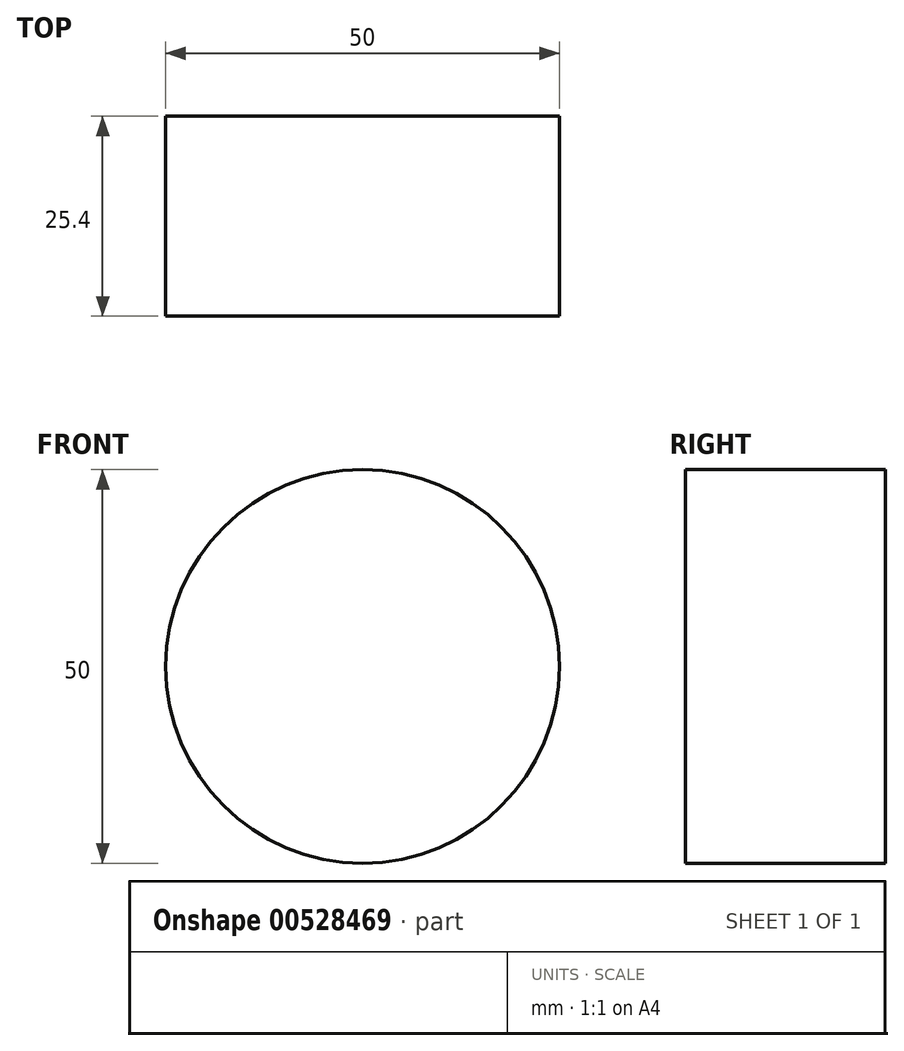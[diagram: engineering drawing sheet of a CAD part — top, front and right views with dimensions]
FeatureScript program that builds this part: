
annotation { "Feature Type Name" : "Feature", "Feature Type Description" : "" }
export const myFeature = defineFeature(function(context is Context, id is Id, definition is map)
    precondition{}
    {
        {
            var Q0;
            Q0=qCreatedBy(makeId("Front.planeOp"),FACE);
            var sketch = newSketch(context, id + "F0", { "sketchPlane" : qUnion([Q0])});
            skCircle(sketch, "E0", {"center": v(29.08, 27.37) * mm, "radius": 25 * mm});
            skSolve(sketch);
        }
        {
            var Q0;
            Q0=makeQuery(id+"F0.imprint","IMPRINT",FACE,{"disambiguationData":[TD([[makeQuery(id+"F0.imprint","IMPRINT",EDGE,{"derivedFrom":sQuery(id+"F0.wireOp",EDGE,"E0")}),1.0]])]});
            extrude(context, id + "F1", {"entities" : qUnion([Q0]), "depth" : 25.4 * mm, "offsetDistance" : 25.4 * mm});
        }
    });
